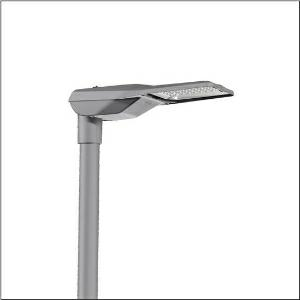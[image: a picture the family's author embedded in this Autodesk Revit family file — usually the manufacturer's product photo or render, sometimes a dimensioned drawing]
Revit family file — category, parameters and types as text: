
# Revit family: streetlight_sl_21_mini___st1_5a_5xe2p33s08gb_ee16
name_source: partatom
category: Lighting Fixtures
units: mm (PartAtom-declared; Revit-internal decimal feet)

## family parameters
Cut with Voids When Loaded = No
Host = Face
Light Source = No
Part Type = Normal
Room Calculation Point = No
Round Connector Dimension = Use Diameter
Shared = No

## types (1)
- --- (1 x LED, 5840 lm, 40.4 W, 3000K)
    Apparent Load = 40 VA
    CIE Flux Codes = 22 53 95 100 100
    Color Rendering = 70
    Color Temperature = 3000K
    Default Elevation = 1800 mm
    Description = Streetlight SL 21 mini, mast luminaire, primary light control with lens, of PMMA, primary optical cover: cover, of toughened safety glass, transparent, light distribution: ST1.5a, light emission: direct distribution, primary light characteristic: asymmetric, installation type: side-entry, post-top, LED, High Power LED, rated luminous flux: 5.840lm, luminous efficacy: 145lm/W, light colour: 730, colour temperature: 3000K, control gear: D4i, control: overheat protection, constant luminous flux control, time-dependent luminous flux control, flexible luminous flux parameterisation, pre-setting: logarithmic dimming characteristic, mains connection: 220..240V, AC, 50/60Hz, start of lifetime: 40W, end of service life: 41W, reduction: 19W, luminaire housing, of diecast aluminium, powder-coated, SITECO metallic grey (DB 702S), corrosivity category C5 high according to DIN EN ISO 12944, please order mast flange separately, inclination adjustable: 0°, 5°, 10°, 15°, sealing non-destructively replaceable, multi-level sealing system, length: 628mm, width: 235mm, height: 110mm, mast flange for spigot size: 42mm (side-entry): 5XC10008XM4, 60/48mm (side-entry/post-top): 5XC10108XM2, 76/60mm (side-entry/post-top): 5XC10108XM1, mounting height: 4..8m, Smart Interface above, protection rating (complete): IP66, insulation class (complete): insulation class II (safety insulation), certification: CE, ENEC, ENEC+, VDE, impact resistance: IK10, permissible operating ambient temperature for outdoor applications: -40..+50°C, standard-compliant lighting for roads and squares, packaging unit: 1 piece

Light Distribution: ST1.5a
    Height = 110 mm
    Lamp = 1 x LED
    Lamp Light Flux = 5840 lm
    Lamp Power = 40.4 W
    Lamp count = 1
    Length = 625 mm
    Luminous efficacy = 145 lm/W
    Manufacturer = Siteco
    ModVariant = No
    Model = 5XE2P33S08GB
    Number of Poles = 1
    OnlyDefault = Yes
    Power Factor = 1
    Product Name = Streetlight SL 21 mini | ST1.5a
    Product group = mast luminaire | pylon top
    ProductGroupID = 6100
    Protection Class = Protection class II
    Protection Degree = IP 66
    RLX_Detail_Level = 1
    RLX_Emergency_Light_Flux = 0 lm
    RLX_Emergency_Type = 0
    RLX_Emergency_Type_DB = No
    RlxData = <blob elided: 29689 chars, md5=0da1e779>
    Socket = socket
    Standby Power = 0 W
    System Light Flux = 5840 lm
    System Power = 40 W
    Type Comments = factory setting: luminous flux: 100 % | dim-lin: 254 | 812 mA
    Type Image = l_1003515.jpg
    URL = http://relux.com
    VarID = @adj_175199
    Voltage = 0 V
    Weight = 0.00 kg
    Width = 234 mm

## geometry (parser evidence)
native form markers: Blend x4, Sweep x10
no freeform markers — native parametric forms only
